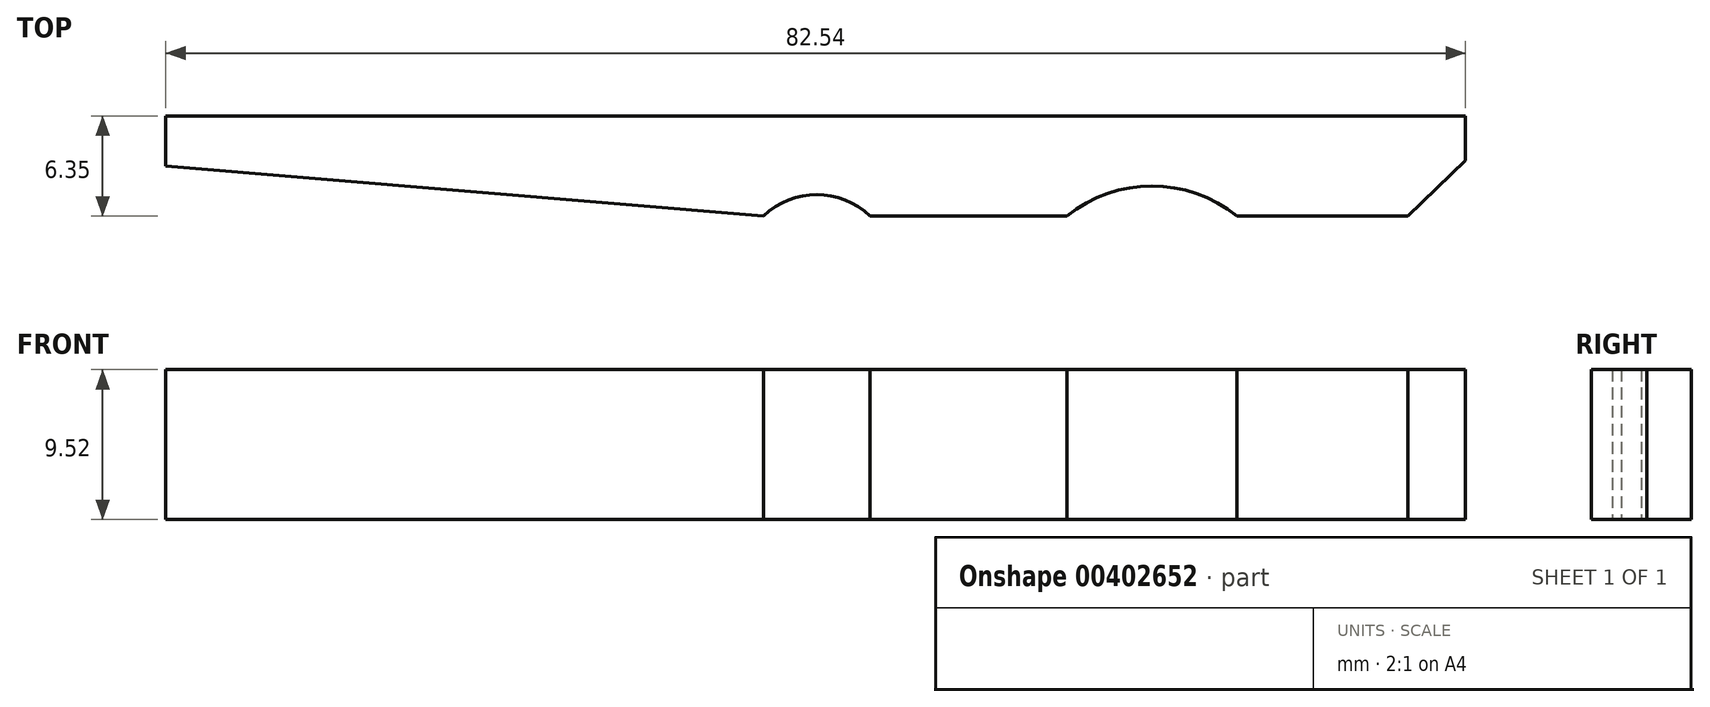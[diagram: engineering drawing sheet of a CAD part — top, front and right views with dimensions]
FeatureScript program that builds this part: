
annotation { "Feature Type Name" : "Feature", "Feature Type Description" : "" }
export const myFeature = defineFeature(function(context is Context, id is Id, definition is map)
    precondition{}
    {
        {
            var Q0;
            Q0=qCreatedBy(makeId("Top.planeOp"),FACE);
            var sketch = newSketch(context, id + "F0", { "sketchPlane" : qUnion([Q0])});
            skLineSegment(sketch, "E0.bottom", {"start": v(37.61, -3.17) * mm, "end": v(26.75, -3.17) * mm});
            skLineSegment(sketch, "E0.top", {"start": v(41.28, 3.18) * mm, "end": v(-41.28, 3.17) * mm});
            skLineSegment(sketch, "E0.left", {"start": v(41.28, 0.34) * mm, "end": v(41.28, 3.18) * mm});
            skLineSegment(sketch, "E0.right", {"start": v(-41.28, 0) * mm, "end": v(-41.28, 3.17) * mm});
            skPoint(sketch, "E0.middle", {"position": v(0, 0) * mm});
            skLineSegment(sketch, "E1", {"start": v(37.61, -3.17) * mm, "end": v(41.27, 0.34) * mm});
            skArc(sketch, "E2", {"start": v(26.75, -3.18) * mm, "mid": v(21.36, -1.27) * mm, "end": v(15.97, -3.18) * mm});
            skLineSegment(sketch, "E3.trimOffspring", {"start": v(15.97, -3.18) * mm, "end": v(3.47, -3.18) * mm});
            skPoint(sketch, "E4.orphan", {"position": v(41.28, -3.17) * mm});
            skLineSegment(sketch, "E5", {"start": v(-41.28, 0) * mm, "end": v(-3.3, -3.18) * mm});
            skPoint(sketch, "E6.orphan", {"position": v(-41.28, -3.18) * mm});
            skArc(sketch, "E7", {"start": v(3.47, -3.18) * mm, "mid": v(0.08, -1.83) * mm, "end": v(-3.3, -3.18) * mm});
            skSolve(sketch);
        }
        {
            var Q0;
            Q0 = qSketchRegion(id + "F0", true);
            extrude(context, id + "F1", {"entities" : qUnion([Q0]), "depth" : 9.52 * mm, "symmetric" : true});
        }
    });
